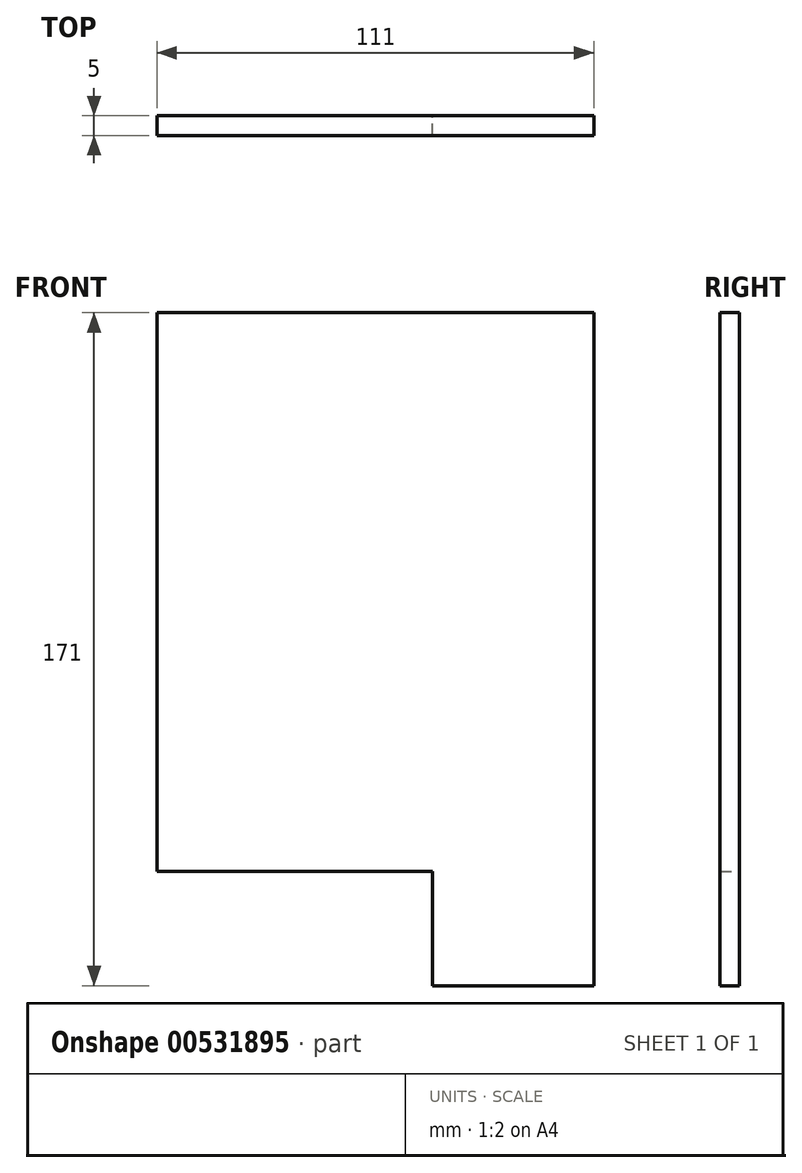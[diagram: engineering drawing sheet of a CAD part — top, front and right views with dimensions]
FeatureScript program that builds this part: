
annotation { "Feature Type Name" : "Feature", "Feature Type Description" : "" }
export const myFeature = defineFeature(function(context is Context, id is Id, definition is map)
    precondition{}
    {
        {
            var Q0;
            Q0=qCreatedBy(makeId("Front.planeOp"),FACE);
            var sketch = newSketch(context, id + "F0", { "sketchPlane" : qUnion([Q0])});
            skLineSegment(sketch, "E0.bottom", {"start": v(55.5, 71) * mm, "end": v(-55.5, 71) * mm});
            skLineSegment(sketch, "E0.top", {"start": v(55.5, -71) * mm, "end": v(-55.5, -71) * mm, "construction": true});
            skLineSegment(sketch, "E0.left", {"start": v(55.5, 71) * mm, "end": v(55.5, -71) * mm});
            skLineSegment(sketch, "E0.right", {"start": v(-55.5, 71) * mm, "end": v(-55.5, -71) * mm, "construction": true});
            skPoint(sketch, "E0.middle", {"position": v(0, 0) * mm});
            skLineSegment(sketch, "E1.bottom", {"start": v(55.5, -71) * mm, "end": v(14.5, -71) * mm, "construction": true});
            skLineSegment(sketch, "E1.top", {"start": v(55.5, -100) * mm, "end": v(14.5, -100) * mm, "construction": true});
            skLineSegment(sketch, "E1.left", {"start": v(55.5, -71) * mm, "end": v(55.5, -100) * mm});
            skLineSegment(sketch, "E1.right", {"start": v(14.5, -71) * mm, "end": v(14.5, -100) * mm});
            skLineSegment(sketch, "E2.bottom", {"start": v(-55.5, 71) * mm, "end": v(-60.5, 71) * mm, "construction": true});
            skLineSegment(sketch, "E2.top", {"start": v(-55.5, -71) * mm, "end": v(-60.5, -71) * mm, "construction": true});
            skLineSegment(sketch, "E2.left", {"start": v(-55.5, 71) * mm, "end": v(-55.5, -71) * mm});
            skLineSegment(sketch, "E2.right", {"start": v(-60.5, 71) * mm, "end": v(-60.5, -71) * mm, "construction": true});
            skLineSegment(sketch, "E3.bottom", {"start": v(-60.5, -71) * mm, "end": v(14.5, -71) * mm});
            skLineSegment(sketch, "E3.top", {"start": v(-60.5, -76) * mm, "end": v(14.5, -76) * mm, "construction": true});
            skLineSegment(sketch, "E3.left", {"start": v(-60.5, -71) * mm, "end": v(-60.5, -76) * mm, "construction": true});
            skLineSegment(sketch, "E3.right", {"start": v(14.5, -71) * mm, "end": v(14.5, -76) * mm, "construction": true});
            skLineSegment(sketch, "E4.bottom", {"start": v(14.5, -76) * mm, "end": v(9.5, -76) * mm, "construction": true});
            skLineSegment(sketch, "E4.top", {"start": v(14.5, -100) * mm, "end": v(9.5, -100) * mm, "construction": true});
            skLineSegment(sketch, "E4.left", {"start": v(14.5, -76) * mm, "end": v(14.5, -100) * mm});
            skLineSegment(sketch, "E4.right", {"start": v(9.5, -76) * mm, "end": v(9.5, -100) * mm, "construction": true});
            skLineSegment(sketch, "E5.bottom", {"start": v(9.5, -100) * mm, "end": v(55.5, -100) * mm});
            skLineSegment(sketch, "E5.top", {"start": v(9.5, -105) * mm, "end": v(55.5, -105) * mm, "construction": true});
            skLineSegment(sketch, "E5.left", {"start": v(9.5, -100) * mm, "end": v(9.5, -105) * mm, "construction": true});
            skLineSegment(sketch, "E5.right", {"start": v(55.5, -100) * mm, "end": v(55.5, -105) * mm, "construction": true});
            skLineSegment(sketch, "E6.bottom", {"start": v(55.5, -105) * mm, "end": v(60.5, -105) * mm, "construction": true});
            skLineSegment(sketch, "E6.top", {"start": v(55.5, 71) * mm, "end": v(60.5, 71) * mm, "construction": true});
            skLineSegment(sketch, "E6.left", {"start": v(55.5, -105) * mm, "end": v(55.5, 71) * mm, "construction": true});
            skLineSegment(sketch, "E6.right", {"start": v(60.5, -105) * mm, "end": v(60.5, 71) * mm, "construction": true});
            skLineSegment(sketch, "E7.bottom", {"start": v(60.5, 71) * mm, "end": v(-60.5, 71) * mm, "construction": true});
            skLineSegment(sketch, "E7.top", {"start": v(60.5, 76) * mm, "end": v(-60.5, 76) * mm, "construction": true});
            skLineSegment(sketch, "E7.left", {"start": v(60.5, 71) * mm, "end": v(60.5, 76) * mm, "construction": true});
            skLineSegment(sketch, "E7.right", {"start": v(-60.5, 71) * mm, "end": v(-60.5, 76) * mm, "construction": true});
            skSolve(sketch);
        }
        {
            var Q0;
            Q0 = qSketchRegion(id + "F0", true);
            extrude(context, id + "F1", {"entities" : qUnion([Q0]), "depth" : 5 * mm, "offsetDistance" : 25 * mm});
        }
    });
